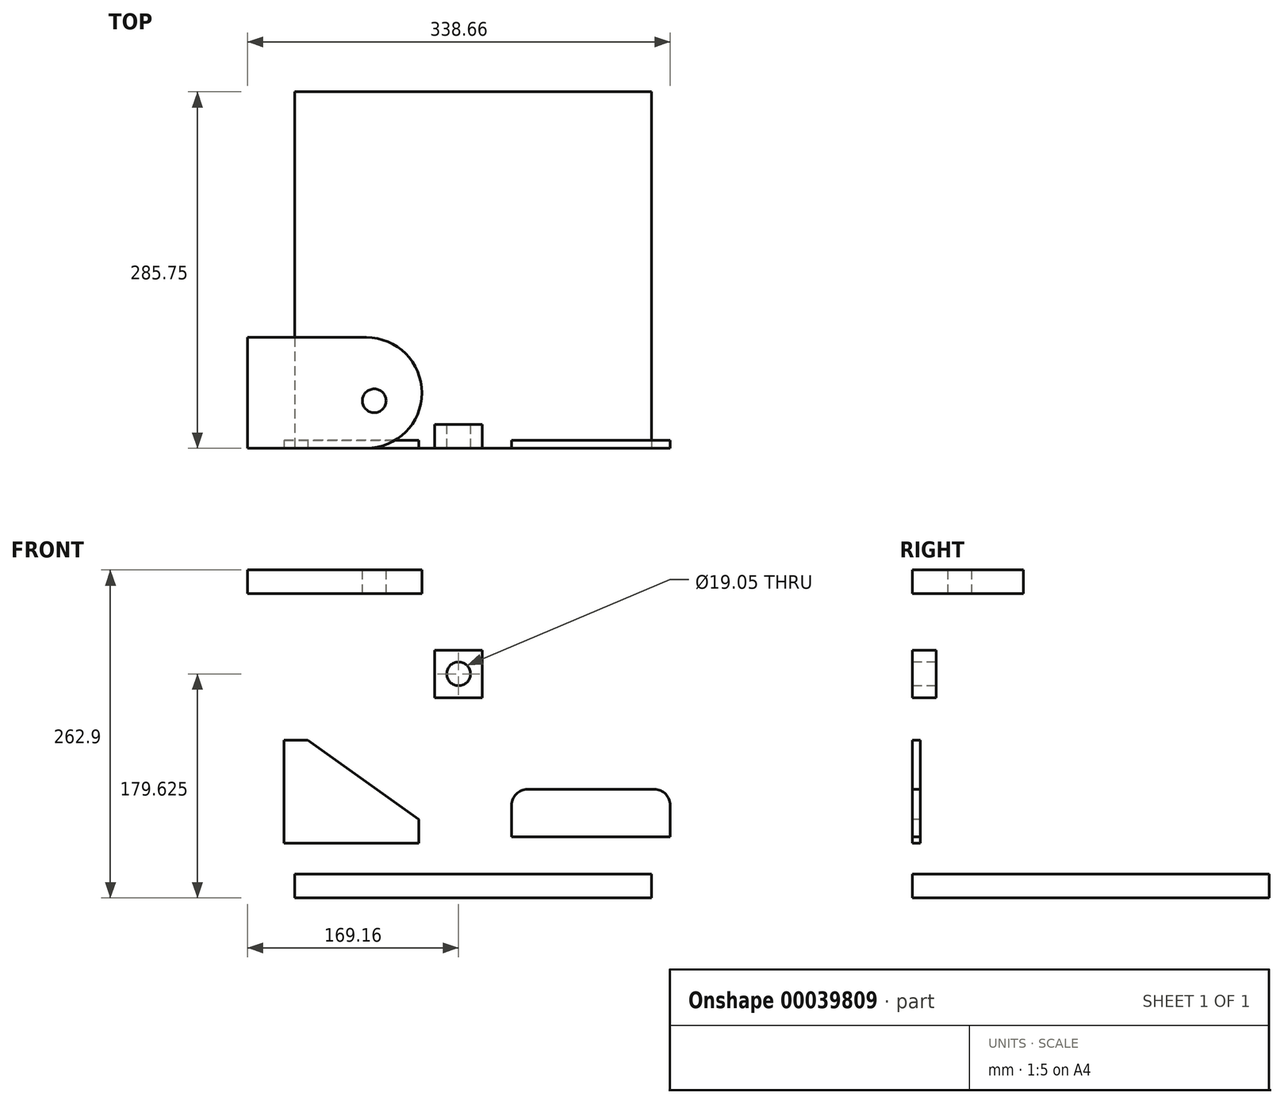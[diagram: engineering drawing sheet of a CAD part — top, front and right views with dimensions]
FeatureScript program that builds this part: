
annotation { "Feature Type Name" : "Feature", "Feature Type Description" : "" }
export const myFeature = defineFeature(function(context is Context, id is Id, definition is map)
    precondition{}
    {
        {
            var Q0;
            Q0=qCreatedBy(makeId("Front.planeOp"),FACE);
            var sketch = newSketch(context, id + "F0", { "sketchPlane" : qUnion([Q0])});
            skLineSegment(sketch, "E0", {"start": v(-70.94, 44.79) * mm, "end": v(-70.94, -37.76) * mm});
            skLineSegment(sketch, "E1", {"start": v(-70.94, -37.76) * mm, "end": v(37, -37.76) * mm});
            skLineSegment(sketch, "E2", {"start": v(37, -37.76) * mm, "end": v(37, -18.71) * mm});
            skLineSegment(sketch, "E3", {"start": v(37, -18.71) * mm, "end": v(-51.9, 44.79) * mm});
            skLineSegment(sketch, "E4", {"start": v(-51.9, 44.79) * mm, "end": v(-70.94, 44.79) * mm});
            skLineSegment(sketch, "E5.bottom", {"start": v(111.24, -32.62) * mm, "end": v(238.24, -32.62) * mm});
            skLineSegment(sketch, "E5.top", {"start": v(111.24, 5.48) * mm, "end": v(238.24, 5.48) * mm});
            skLineSegment(sketch, "E5.left", {"start": v(111.24, -32.62) * mm, "end": v(111.24, 5.48) * mm});
            skLineSegment(sketch, "E5.right", {"start": v(238.24, -32.62) * mm, "end": v(238.24, 5.48) * mm});
            skSolve(sketch);
        }
        {
            var Q0;
            Q0=makeQuery(id+"F0.imprint","IMPRINT",FACE,{"disambiguationData":[TD([[makeQuery(id+"F0.imprint","IMPRINT",EDGE,{"derivedFrom":sQuery(id+"F0.wireOp",EDGE,"E0")}),1.0]])]});
            var Q1;
            Q1=makeQuery(id+"F0.imprint","IMPRINT",FACE,{"disambiguationData":[TD([[makeQuery(id+"F0.imprint","IMPRINT",EDGE,{"derivedFrom":sQuery(id+"F0.wireOp",EDGE,"E5.bottom")}),1.0]])]});
            extrude(context, id + "F1", {"entities" : qUnion([Q0, Q1]), "oppositeDirection" : true, "depth" : 6.35 * mm});
        }
        {
            var Q0;
            Q0=makeQuery(id+"F1.opExtrude","SWEPT_EDGE",EDGE,{"disambiguationData":[OSD([sQuery(id+"F0.wireOp",EDGE,"E5.top"),sQuery(id+"F0.wireOp",EDGE,"E5.right")])]});
            var Q1;
            Q1=makeQuery(id+"F1.opExtrude","SWEPT_EDGE",EDGE,{"disambiguationData":[OSD([sQuery(id+"F0.wireOp",EDGE,"E5.top"),sQuery(id+"F0.wireOp",EDGE,"E5.left")])]});
            fillet(context, id + "F2", {"entities" : qUnion([Q0, Q1]), "radius" : 12.7 * mm, "tangentPropagation" : true, "allowEdgeOverflow" : false});
        }
        {
            var Q0;
            Q0=qCreatedBy(makeId("Front.planeOp"),FACE);
            var sketch = newSketch(context, id + "F3", { "sketchPlane" : qUnion([Q0])});
            skLineSegment(sketch, "E6.bottom", {"start": v(-62.49, -81.58) * mm, "end": v(223.26, -81.58) * mm});
            skLineSegment(sketch, "E6.top", {"start": v(-62.49, -62.53) * mm, "end": v(223.26, -62.53) * mm});
            skLineSegment(sketch, "E6.left", {"start": v(-62.49, -81.58) * mm, "end": v(-62.49, -62.53) * mm});
            skLineSegment(sketch, "E6.right", {"start": v(223.26, -81.58) * mm, "end": v(223.26, -62.53) * mm});
            skSolve(sketch);
        }
        {
            var Q0;
            Q0=makeQuery(id+"F3.imprint","IMPRINT",FACE,{"disambiguationData":[TD([[makeQuery(id+"F3.imprint","IMPRINT",EDGE,{"derivedFrom":sQuery(id+"F3.wireOp",EDGE,"E6.bottom")}),1.0]])]});
            extrude(context, id + "F4", {"entities" : qUnion([Q0]), "oppositeDirection" : true, "depth" : 285.75 * mm});
        }
        {
            var Q0;
            Q0=qCreatedBy(makeId("Front.planeOp"),FACE);
            var sketch = newSketch(context, id + "F5", { "sketchPlane" : qUnion([Q0])});
            skLineSegment(sketch, "E7.rect.bottom", {"start": v(87.79, 79) * mm, "end": v(49.69, 79) * mm});
            skLineSegment(sketch, "E7.rect.top", {"start": v(87.79, 117.1) * mm, "end": v(49.69, 117.1) * mm});
            skLineSegment(sketch, "E7.rect.left", {"start": v(87.79, 79) * mm, "end": v(87.79, 117.1) * mm});
            skLineSegment(sketch, "E7.rect.right", {"start": v(49.69, 79) * mm, "end": v(49.69, 117.1) * mm});
            skPoint(sketch, "E7.rect.middle", {"position": v(68.74, 98.05) * mm});
            skCircle(sketch, "E8", {"center": v(68.74, 98.05) * mm, "radius": 9.53 * mm});
            skSolve(sketch);
        }
        {
            var Q0;
            Q0=makeQuery(id+"F5.imprint","IMPRINT",FACE,{"disambiguationData":[TD([[makeQuery(id+"F5.imprint","IMPRINT",EDGE,{"derivedFrom":sQuery(id+"F5.wireOp",EDGE,"E7.rect.bottom")}),-1.0]])]});
            extrude(context, id + "F6", {"entities" : qUnion([Q0]), "oppositeDirection" : true, "depth" : 19.05 * mm});
        }
        {
            var Q0;
            Q0=qCreatedBy(makeId("Front.planeOp"),FACE);
            var sketch = newSketch(context, id + "F7", { "sketchPlane" : qUnion([Q0])});
            skLineSegment(sketch, "E9.rect.bottom", {"start": v(39.28, 162.27) * mm, "end": v(-100.42, 162.27) * mm});
            skLineSegment(sketch, "E9.rect.top", {"start": v(39.28, 181.32) * mm, "end": v(-100.42, 181.32) * mm});
            skLineSegment(sketch, "E9.rect.left", {"start": v(39.28, 162.27) * mm, "end": v(39.28, 181.32) * mm});
            skLineSegment(sketch, "E9.rect.right", {"start": v(-100.42, 162.27) * mm, "end": v(-100.42, 181.32) * mm});
            skPoint(sketch, "E9.rect.middle", {"position": v(-30.57, 171.8) * mm});
            skSolve(sketch);
        }
        {
            var Q0;
            Q0=makeQuery(id+"F7.imprint","IMPRINT",FACE,{"disambiguationData":[TD([[makeQuery(id+"F7.imprint","IMPRINT",EDGE,{"derivedFrom":sQuery(id+"F7.wireOp",EDGE,"E9.rect.bottom")}),-1.0]])]});
            extrude(context, id + "F8", {"entities" : qUnion([Q0]), "oppositeDirection" : true, "depth" : 88.9 * mm});
        }
        {
            var Q0;
            Q0=makeQuery(id+"F8.opExtrude","SWEPT_FACE",FACE,{"disambiguationData":[OSD([sQuery(id+"F7.wireOp",EDGE,"E9.rect.top")])]});
            var sketch = newSketch(context, id + "F9", { "sketchPlane" : qUnion([Q0])});
            skCircle(sketch, "E10", {"center": v(1.18, 38.1) * mm, "radius": 9.53 * mm});
            skSolve(sketch);
        }
        {
            var Q0;
            Q0=makeQuery(id+"F9.imprint","IMPRINT",FACE,{"disambiguationData":[TD([[makeQuery(id+"F9.imprint","IMPRINT",EDGE,{"derivedFrom":sQuery(id+"F9.wireOp",EDGE,"E10")}),1.0]])]});
            extrude(context, id + "F10", {"entities" : qUnion([Q0]), "operationType" : NewBodyOperationType.REMOVE, "oppositeDirection" : true, "depth" : 25.4 * mm});
        }
        {
            var Q0;
            Q0=makeQuery(id+"F8.opExtrude","CAP_EDGE",EDGE,{"disambiguationData":[OSD([sQuery(id+"F7.wireOp",EDGE,"E9.rect.left")])],"isStart":true});
            var Q1;
            Q1=makeQuery(id+"F8.opExtrude","CAP_EDGE",EDGE,{"disambiguationData":[OSD([sQuery(id+"F7.wireOp",EDGE,"E9.rect.left")])],"isStart":false});
            fillet(context, id + "F11", {"entities" : qUnion([Q0, Q1]), "radius" : 44.45 * mm, "tangentPropagation" : true, "allowEdgeOverflow" : false});
        }
    });
